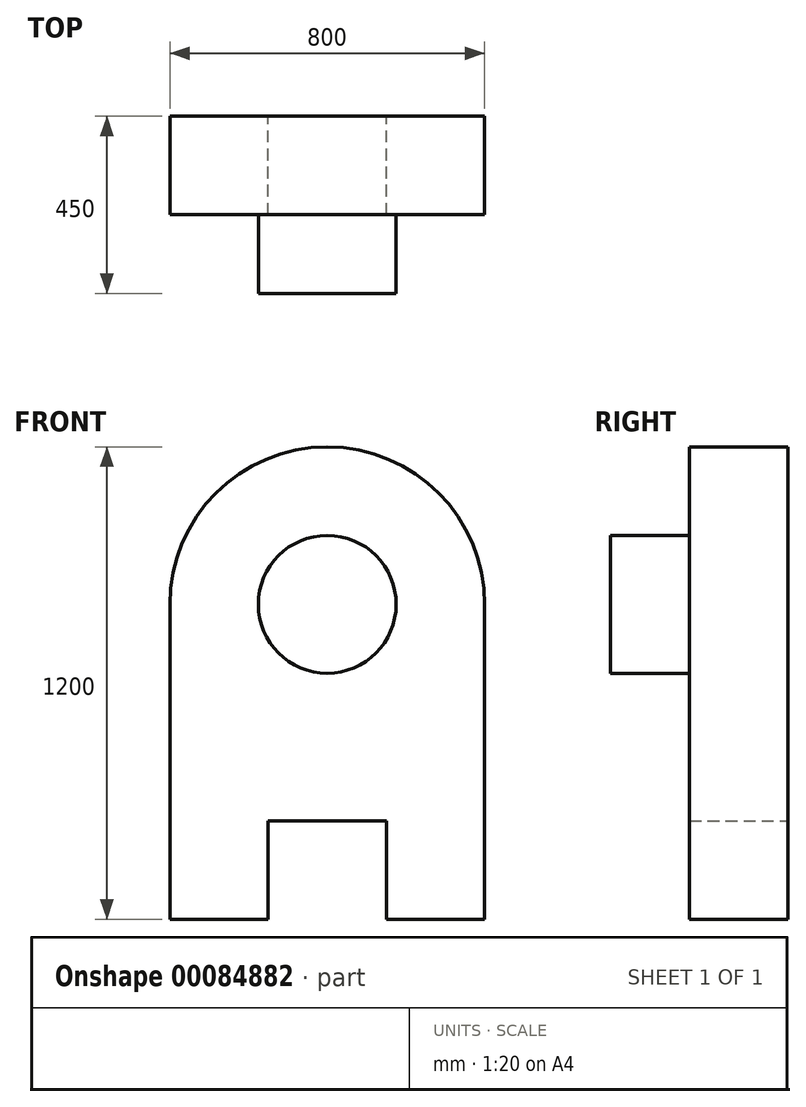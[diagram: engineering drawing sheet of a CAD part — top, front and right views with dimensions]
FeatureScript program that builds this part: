
annotation { "Feature Type Name" : "Feature", "Feature Type Description" : "" }
export const myFeature = defineFeature(function(context is Context, id is Id, definition is map)
    precondition{}
    {
        {
            var Q0;
            Q0=qCreatedBy(makeId("Front.planeOp"),FACE);
            var sketch = newSketch(context, id + "F0", { "sketchPlane" : qUnion([Q0])});
            skArc(sketch, "E0", {"start": v(400, 0) * mm, "mid": v(0, 400) * mm, "end": v(-400, 0) * mm});
            skLineSegment(sketch, "E1.bottom", {"start": v(-400, -800) * mm, "end": v(-150, -800) * mm});
            skLineSegment(sketch, "E1.left", {"start": v(-400, -800) * mm, "end": v(-400, 0) * mm});
            skLineSegment(sketch, "E1.right", {"start": v(400, -800) * mm, "end": v(400, 0) * mm});
            skPoint(sketch, "E1.middle", {"position": v(0, -400) * mm});
            skPoint(sketch, "E2.orphan", {"position": v(400, 0) * mm});
            skPoint(sketch, "E3.orphan", {"position": v(-400, 0) * mm});
            skLineSegment(sketch, "E4.bottom", {"start": v(-150, -550) * mm, "end": v(150, -550) * mm});
            skLineSegment(sketch, "E4.left", {"start": v(-150, -550) * mm, "end": v(-150, -800) * mm});
            skLineSegment(sketch, "E4.right", {"start": v(150, -550) * mm, "end": v(150, -800) * mm});
            skPoint(sketch, "E4.middle", {"position": v(0, -800) * mm});
            skPoint(sketch, "E5.orphan", {"position": v(150, -1050) * mm});
            skPoint(sketch, "E6.orphan", {"position": v(-150, -1050) * mm});
            skLineSegment(sketch, "E7.trimOffspring", {"start": v(150, -800) * mm, "end": v(400, -800) * mm});
            skSolve(sketch);
        }
        {
            var Q0;
            Q0 = qSketchRegion(id + "F0", true);
            extrude(context, id + "F1", {"entities" : qUnion([Q0]), "depth" : 250 * mm});
        }
        {
            var Q0;
            Q0=makeQuery(id+"F1.opExtrude","CAP_FACE",FACE,{"disambiguationData":[OSD([sQuery(id+"F0.wireOp",EDGE,"E0"),sQuery(id+"F0.wireOp",EDGE,"E1.bottom"),sQuery(id+"F0.wireOp",EDGE,"E1.left"),sQuery(id+"F0.wireOp",EDGE,"E1.right"),sQuery(id+"F0.wireOp",EDGE,"E4.bottom"),sQuery(id+"F0.wireOp",EDGE,"E4.left"),sQuery(id+"F0.wireOp",EDGE,"E4.right"),sQuery(id+"F0.wireOp",EDGE,"E7.trimOffspring")])],"isStart":false});
            var sketch = newSketch(context, id + "F2", { "sketchPlane" : qUnion([Q0])});
            skCircle(sketch, "E8", {"center": v(0, 0) * mm, "radius": 175 * mm});
            skSolve(sketch);
        }
        {
            var Q0;
            Q0 = qSketchRegion(id + "F2", true);
            extrude(context, id + "F3", {"entities" : qUnion([Q0]), "operationType" : NewBodyOperationType.ADD, "depth" : 200 * mm});
        }
    });
